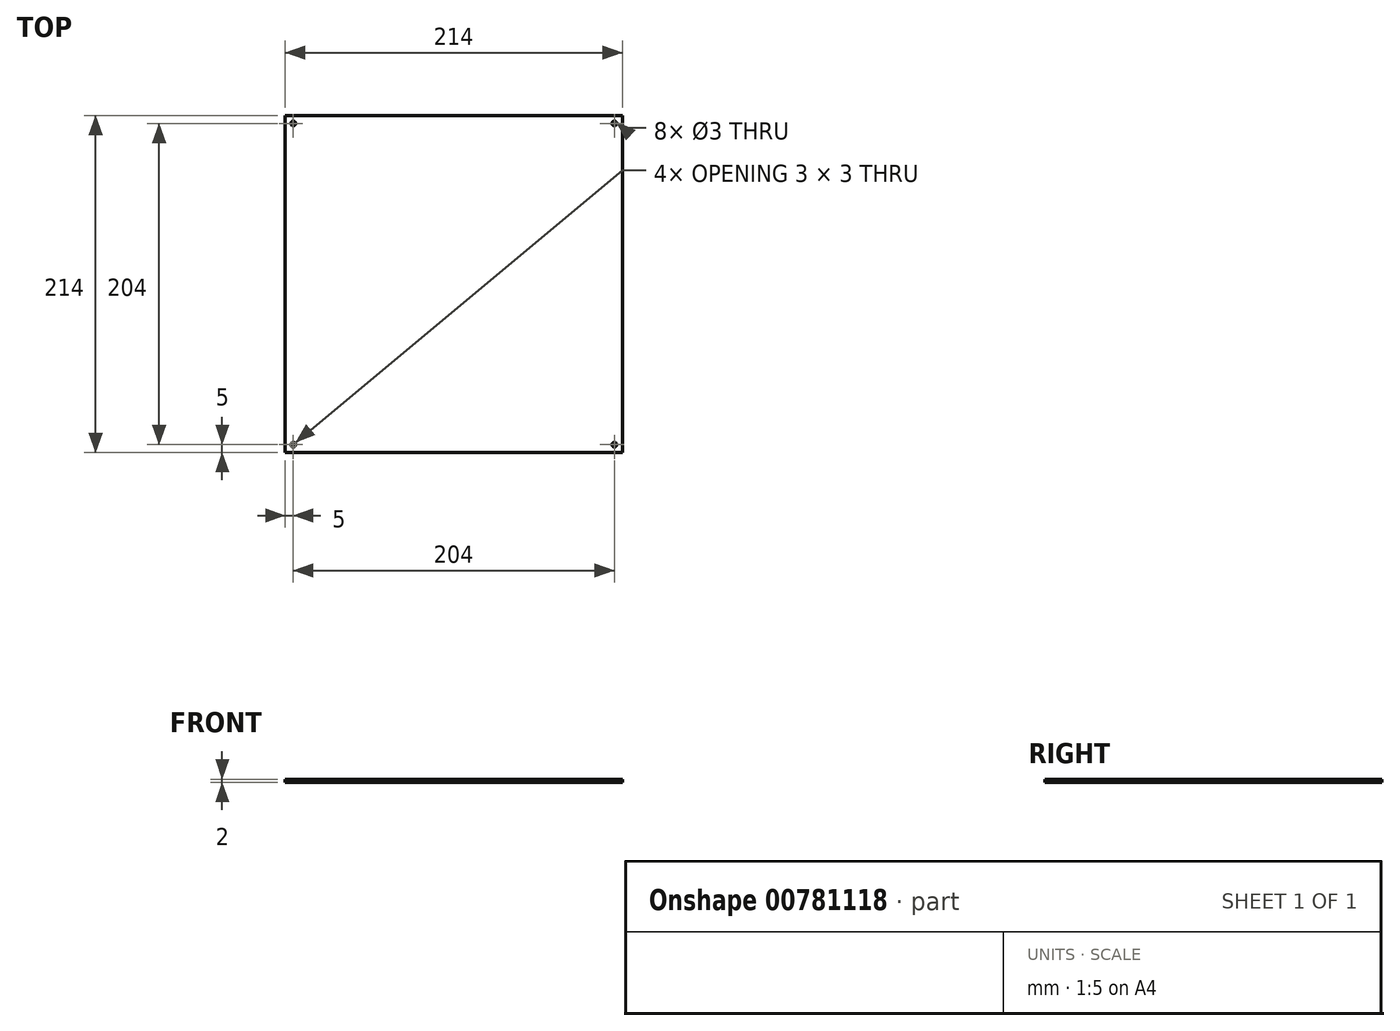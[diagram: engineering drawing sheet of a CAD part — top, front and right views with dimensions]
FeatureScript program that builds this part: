
annotation { "Feature Type Name" : "Feature", "Feature Type Description" : "" }
export const myFeature = defineFeature(function(context is Context, id is Id, definition is map)
    precondition{}
    {
        {
            var Q0;
            Q0=qCreatedBy(makeId("Top.planeOp"),FACE);
            var sketch = newSketch(context, id + "F0", { "sketchPlane" : qUnion([Q0])});
            skLineSegment(sketch, "E0.bottom", {"start": v(107, -107) * mm, "end": v(-107, -107) * mm});
            skLineSegment(sketch, "E0.top", {"start": v(107, 107) * mm, "end": v(-107, 107) * mm});
            skLineSegment(sketch, "E0.left", {"start": v(107, -107) * mm, "end": v(107, 107) * mm});
            skLineSegment(sketch, "E0.right", {"start": v(-107, -107) * mm, "end": v(-107, 107) * mm});
            skPoint(sketch, "E0.middle", {"position": v(0, 0) * mm});
            skLineSegment(sketch, "E1.bottom", {"start": v(102, -102) * mm, "end": v(-102, -102) * mm, "construction": true});
            skLineSegment(sketch, "E1.top", {"start": v(102, 102) * mm, "end": v(-102, 102) * mm, "construction": true});
            skLineSegment(sketch, "E1.left", {"start": v(102, -102) * mm, "end": v(102, 102) * mm, "construction": true});
            skLineSegment(sketch, "E1.right", {"start": v(-102, -102) * mm, "end": v(-102, 102) * mm, "construction": true});
            skSolve(sketch);
        }
        {
            var Q0;
            Q0 = qSketchRegion(id + "F0", true);
            extrude(context, id + "F1", {"entities" : qUnion([Q0]), "depth" : 2 * mm, "offsetDistance" : 25 * mm});
        }
        {
            var Q0;
            Q0=sQuery(id+"F0.wireOp",VERTEX,"E1.top.end");
            var Q1;
            Q1=sQuery(id+"F0.wireOp",VERTEX,"E1.top.start");
            var Q2;
            Q2=sQuery(id+"F0.wireOp",VERTEX,"E1.bottom.start");
            var Q3;
            Q3=sQuery(id+"F0.wireOp",VERTEX,"E1.bottom.end");
            var Q4;
            Q4=makeQuery(id+"F1.opExtrude","SWEPT_BODY",BODY,{"disambiguationData":[OSD([sQuery(id+"F0.wireOp",EDGE,"E0.bottom"),sQuery(id+"F0.wireOp",EDGE,"E0.top"),sQuery(id+"F0.wireOp",EDGE,"E0.left"),sQuery(id+"F0.wireOp",EDGE,"E0.right")])]});
            hole(context, id + "F2", {"style" : HoleStyle.SIMPLE, "endStyle" : HoleEndStyle.THROUGH, "oppositeDirection" : true, "holeDiameter" : 3 * mm, "majorDiameter" : 5 * mm, "isTappedThrough" : true, "tappedDepth" : 12 * mm, "tapClearance" : 3, "locations" : qUnion([Q0, Q1, Q2, Q3]), "scope" : qUnion([Q4])});
        }
    });
